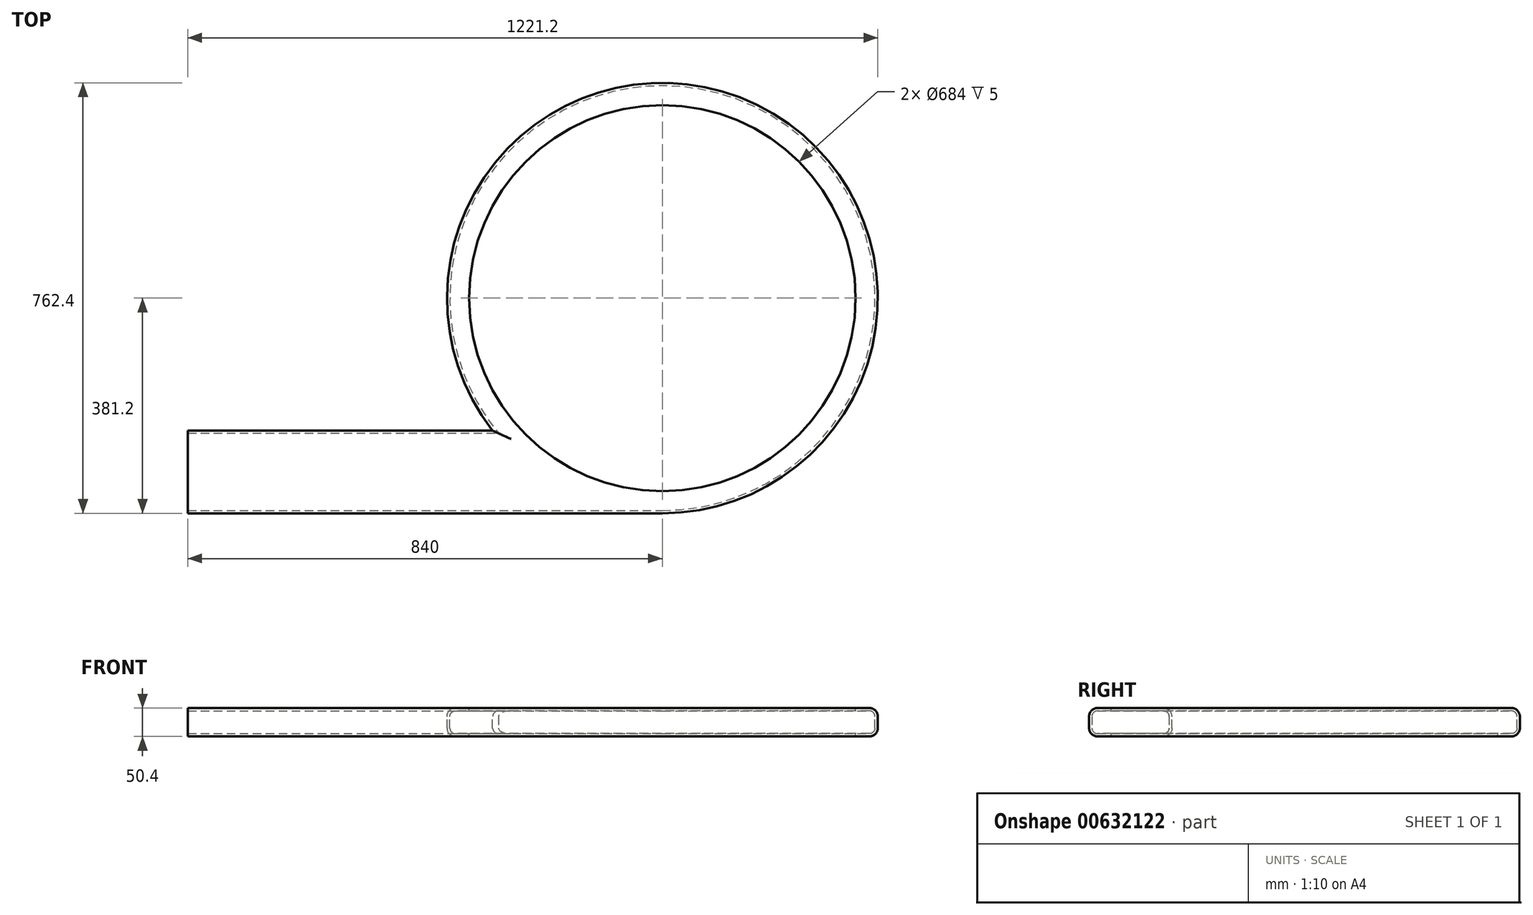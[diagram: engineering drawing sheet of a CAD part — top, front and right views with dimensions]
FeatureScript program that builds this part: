
annotation { "Feature Type Name" : "Feature", "Feature Type Description" : "" }
export const myFeature = defineFeature(function(context is Context, id is Id, definition is map)
    precondition{}
    {
        {
            var Q0;
            Q0=qCreatedBy(makeId("Top.planeOp"),FACE);
            var sketch = newSketch(context, id + "F0", { "sketchPlane" : qUnion([Q0])});
            skPoint(sketch, "E0", {"position": v(120, 0) * mm});
            skPoint(sketch, "E1", {"position": v(120.43, 3.39) * mm});
            skPoint(sketch, "E2", {"position": v(120.87, 6.78) * mm});
            skPoint(sketch, "E3", {"position": v(121.31, 10.17) * mm});
            skPoint(sketch, "E4", {"position": v(121.75, 13.57) * mm});
            skPoint(sketch, "E5", {"position": v(122.19, 16.98) * mm});
            skPoint(sketch, "E6", {"position": v(122.63, 20.37) * mm});
            skPoint(sketch, "E7", {"position": v(124.7, 30.21) * mm});
            skPoint(sketch, "E8", {"position": v(126.32, 40.24) * mm});
            skPoint(sketch, "E9", {"position": v(127.2, 50.5) * mm});
            skPoint(sketch, "E10", {"position": v(127.28, 60.98) * mm});
            skPoint(sketch, "E11", {"position": v(126.55, 71.6) * mm});
            skPoint(sketch, "E12", {"position": v(125, 82.33) * mm});
            skPoint(sketch, "E13", {"position": v(122.6, 93.1) * mm});
            skPoint(sketch, "E14", {"position": v(119.4, 103.82) * mm});
            skPoint(sketch, "E15", {"position": v(115.32, 114.48) * mm});
            skPoint(sketch, "E16", {"position": v(110.46, 124.94) * mm});
            skPoint(sketch, "E17", {"position": v(104.8, 135.2) * mm});
            skPoint(sketch, "E18", {"position": v(98.37, 145.13) * mm});
            skPoint(sketch, "E19", {"position": v(91.24, 154.7) * mm});
            skPoint(sketch, "E20", {"position": v(83.43, 163.88) * mm});
            skPoint(sketch, "E21", {"position": v(74.97, 172.59) * mm});
            skPoint(sketch, "E22", {"position": v(65.98, 180.79) * mm});
            skPoint(sketch, "E23", {"position": v(56.5, 188.45) * mm});
            skPoint(sketch, "E24", {"position": v(46.55, 195.56) * mm});
            skPoint(sketch, "E25", {"position": v(43.8, 199.07) * mm});
            skPoint(sketch, "E26", {"position": v(41.13, 202.54) * mm});
            skPoint(sketch, "E27", {"position": v(38.47, 205.97) * mm});
            skSolve(sketch);
        }
        {
            var Q0;
            Q0=qCreatedBy(makeId("Top.planeOp"),FACE);
            var sketch = newSketch(context, id + "F1", { "sketchPlane" : qUnion([Q0])});
            skPoint(sketch, "E28", {"position": v(120, 0) * mm});
            skPoint(sketch, "E29", {"position": v(122.73, 2.49) * mm});
            skPoint(sketch, "E30", {"position": v(124.8, 5.43) * mm});
            skPoint(sketch, "E31", {"position": v(126.44, 9.06) * mm});
            skPoint(sketch, "E32", {"position": v(128.14, 12.11) * mm});
            skPoint(sketch, "E33", {"position": v(129.88, 15.23) * mm});
            skPoint(sketch, "E34", {"position": v(131.67, 18.41) * mm});
            skPoint(sketch, "E35", {"position": v(134.5, 28.24) * mm});
            skPoint(sketch, "E36", {"position": v(136.25, 39.02) * mm});
            skPoint(sketch, "E37", {"position": v(137.19, 50.04) * mm});
            skPoint(sketch, "E38", {"position": v(137.28, 61.26) * mm});
            skPoint(sketch, "E39", {"position": v(136.5, 72.67) * mm});
            skPoint(sketch, "E40", {"position": v(134.83, 84.12) * mm});
            skPoint(sketch, "E41", {"position": v(132.28, 95.62) * mm});
            skPoint(sketch, "E42", {"position": v(128.85, 107.05) * mm});
            skPoint(sketch, "E43", {"position": v(124.54, 118.35) * mm});
            skPoint(sketch, "E44", {"position": v(119.36, 129.49) * mm});
            skPoint(sketch, "E45", {"position": v(113.38, 140.32) * mm});
            skPoint(sketch, "E46", {"position": v(106.6, 150.83) * mm});
            skPoint(sketch, "E47", {"position": v(99.05, 160.94) * mm});
            skPoint(sketch, "E48", {"position": v(90.82, 170.6) * mm});
            skPoint(sketch, "E49", {"position": v(81.96, 179.76) * mm});
            skPoint(sketch, "E50", {"position": v(72.5, 188.38) * mm});
            skPoint(sketch, "E51", {"position": v(62.53, 196.42) * mm});
            skPoint(sketch, "E52", {"position": v(52.12, 203.86) * mm});
            skPoint(sketch, "E53", {"position": v(47.32, 204.95) * mm});
            skPoint(sketch, "E54", {"position": v(42.9, 205.94) * mm});
            skPoint(sketch, "E55", {"position": v(38.97, 206.83) * mm});
            skSolve(sketch);
        }
        {
            var Q0;
            Q0=qCreatedBy(makeId("Top.planeOp"),FACE);
            var sketch = newSketch(context, id + "F2", { "sketchPlane" : qUnion([Q0])});
            skPoint(sketch, "E56", {"position": v(120, 0) * mm});
            skPoint(sketch, "E57", {"position": v(120.43, 3.39) * mm});
            skPoint(sketch, "E58", {"position": v(120.87, 6.78) * mm});
            skPoint(sketch, "E59", {"position": v(121.31, 10.17) * mm});
            skPoint(sketch, "E60", {"position": v(121.75, 13.57) * mm});
            skPoint(sketch, "E61", {"position": v(122.19, 16.98) * mm});
            skPoint(sketch, "E62", {"position": v(122.63, 20.37) * mm});
            skPoint(sketch, "E63", {"position": v(124.7, 30.21) * mm});
            skPoint(sketch, "E64", {"position": v(126.32, 40.24) * mm});
            skPoint(sketch, "E65", {"position": v(127.2, 50.5) * mm});
            skPoint(sketch, "E66", {"position": v(127.28, 60.98) * mm});
            skPoint(sketch, "E67", {"position": v(126.55, 71.6) * mm});
            skPoint(sketch, "E68", {"position": v(125, 82.33) * mm});
            skPoint(sketch, "E69", {"position": v(122.6, 93.1) * mm});
            skPoint(sketch, "E70", {"position": v(119.4, 103.82) * mm});
            skPoint(sketch, "E71", {"position": v(115.32, 114.48) * mm});
            skPoint(sketch, "E72", {"position": v(110.46, 124.94) * mm});
            skPoint(sketch, "E73", {"position": v(104.8, 135.2) * mm});
            skPoint(sketch, "E74", {"position": v(98.37, 145.13) * mm});
            skPoint(sketch, "E75", {"position": v(91.24, 154.7) * mm});
            skPoint(sketch, "E76", {"position": v(83.43, 163.88) * mm});
            skPoint(sketch, "E77", {"position": v(74.97, 172.59) * mm});
            skPoint(sketch, "E78", {"position": v(65.98, 180.79) * mm});
            skPoint(sketch, "E79", {"position": v(56.5, 188.45) * mm});
            skPoint(sketch, "E80", {"position": v(46.55, 195.56) * mm});
            skPoint(sketch, "E81", {"position": v(43.8, 199.07) * mm});
            skPoint(sketch, "E82", {"position": v(41.13, 202.54) * mm});
            skPoint(sketch, "E83", {"position": v(38.47, 205.97) * mm});
            skFitSpline(sketch, "E84", {"points": [v(38.47, 205.97) * mm, v(41.13, 202.54) * mm, v(43.8, 199.07) * mm, v(46.55, 195.56) * mm, v(56.5, 188.45) * mm, v(65.98, 180.79) * mm, v(74.97, 172.59) * mm, v(83.43, 163.88) * mm, v(91.24, 154.7) * mm, v(98.37, 145.13) * mm, v(104.8, 135.2) * mm, v(110.46, 124.94) * mm, v(115.32, 114.48) * mm, v(119.4, 103.82) * mm, v(122.6, 93.1) * mm, v(125, 82.33) * mm, v(126.55, 71.6) * mm, v(127.28, 60.98) * mm, v(127.2, 50.5) * mm, v(126.32, 40.24) * mm, v(124.7, 30.21) * mm, v(122.63, 20.37) * mm, v(122.19, 16.98) * mm, v(121.75, 13.57) * mm, v(121.31, 10.17) * mm, v(120.87, 6.78) * mm, v(120.43, 3.39) * mm, v(120, 0) * mm], "startDerivative": vector(97.9, -127.8) * mm, "endDerivative": vector(-18.24, -142.78) * mm});
            skPoint(sketch, "E85", {"position": v(38.97, 206.83) * mm});
            skPoint(sketch, "E86", {"position": v(42.9, 205.94) * mm});
            skPoint(sketch, "E87", {"position": v(47.32, 204.95) * mm});
            skPoint(sketch, "E88", {"position": v(52.12, 203.86) * mm});
            skPoint(sketch, "E89", {"position": v(62.53, 196.42) * mm});
            skPoint(sketch, "E90", {"position": v(72.5, 188.38) * mm});
            skPoint(sketch, "E91", {"position": v(81.96, 179.76) * mm});
            skPoint(sketch, "E92", {"position": v(90.82, 170.6) * mm});
            skPoint(sketch, "E93", {"position": v(99.05, 160.94) * mm});
            skPoint(sketch, "E94", {"position": v(106.6, 150.83) * mm});
            skPoint(sketch, "E95", {"position": v(113.38, 140.32) * mm});
            skPoint(sketch, "E96", {"position": v(119.36, 129.49) * mm});
            skPoint(sketch, "E97", {"position": v(124.54, 118.35) * mm});
            skPoint(sketch, "E98", {"position": v(128.85, 107.05) * mm});
            skPoint(sketch, "E99", {"position": v(132.28, 95.62) * mm});
            skPoint(sketch, "E100", {"position": v(134.83, 84.12) * mm});
            skPoint(sketch, "E101", {"position": v(136.5, 72.67) * mm});
            skPoint(sketch, "E102", {"position": v(137.28, 61.26) * mm});
            skPoint(sketch, "E103", {"position": v(137.19, 50.04) * mm});
            skPoint(sketch, "E104", {"position": v(136.25, 39.02) * mm});
            skPoint(sketch, "E105", {"position": v(134.5, 28.24) * mm});
            skPoint(sketch, "E106", {"position": v(131.67, 18.41) * mm});
            skPoint(sketch, "E107", {"position": v(129.88, 15.23) * mm});
            skPoint(sketch, "E108", {"position": v(128.14, 12.11) * mm});
            skPoint(sketch, "E109", {"position": v(126.44, 9.06) * mm});
            skPoint(sketch, "E110", {"position": v(124.8, 5.43) * mm});
            skPoint(sketch, "E111", {"position": v(122.73, 2.49) * mm});
            skLineSegment(sketch, "E112", {"start": v(38.97, 206.83) * mm, "end": v(42.9, 205.94) * mm});
            skLineSegment(sketch, "E113", {"start": v(42.9, 205.94) * mm, "end": v(47.32, 204.95) * mm});
            skLineSegment(sketch, "E114", {"start": v(47.32, 204.95) * mm, "end": v(52.12, 203.86) * mm});
            skLineSegment(sketch, "E115", {"start": v(38.97, 206.83) * mm, "end": v(38.47, 205.97) * mm});
            skFitSpline(sketch, "E116", {"points": [v(120, 0) * mm, v(122.73, 2.49) * mm, v(124.8, 5.43) * mm, v(131.67, 18.41) * mm, v(134.5, 28.24) * mm, v(136.25, 39.02) * mm, v(137.19, 50.04) * mm, v(137.28, 61.26) * mm, v(136.5, 72.67) * mm, v(134.83, 84.12) * mm, v(132.28, 95.62) * mm, v(128.85, 107.05) * mm, v(124.54, 118.35) * mm, v(119.36, 129.49) * mm, v(113.38, 140.32) * mm, v(106.6, 150.83) * mm, v(99.05, 160.94) * mm, v(90.82, 170.6) * mm, v(81.96, 179.76) * mm, v(72.5, 188.38) * mm, v(62.53, 196.42) * mm, v(52.12, 203.86) * mm], "startDerivative": vector(108.95, 92.2) * mm, "endDerivative": vector(-205.44, 143.17) * mm});
            skSolve(sketch);
        }
        {
            var Q0;
            Q0 = qSketchRegion(id + "F2", true);
            extrude(context, id + "F3", {"entities" : qUnion([Q0]), "depth" : 20.2 * mm, "offsetDistance" : 25 * mm, "hasSecondDirection" : true, "secondDirectionOppositeDirection" : true, "secondDirectionDepth" : 20.2 * mm});
        }
        {
            var Q0;
            Q0=qCreatedBy(makeId("Right.planeOp"),FACE);
            var sketch = newSketch(context, id + "F4", { "sketchPlane" : qUnion([Q0])});
            skLineSegment(sketch, "E117", {"start": v(0, 0) * mm, "end": v(0, 50) * mm, "construction": true});
            skSolve(sketch);
        }
        {
            var Q0;
            Q0=makeQuery(id+"F3.opExtrude","SWEPT_EDGE",EDGE,{"disambiguationData":[OSD([sQuery(id+"F2.wireOp",EDGE,"E84"),sQuery(id+"F2.wireOp",EDGE,"E115")])]});
            var Q1;
            Q1=makeQuery(id+"F3.opExtrude","SWEPT_EDGE",EDGE,{"disambiguationData":[OSD([sQuery(id+"F2.wireOp",EDGE,"E112"),sQuery(id+"F2.wireOp",EDGE,"E115")])]});
            fillet(context, id + "F5", {"entities" : qUnion([Q0, Q1]), "radius" : 0.75 * mm, "tangentPropagation" : true, "allowEdgeOverflow" : false});
        }
        {
            var Q0;
            Q0=makeQuery(id+"F3.opExtrude","SWEPT_BODY",BODY,{"disambiguationData":[OSD([sQuery(id+"F2.wireOp",EDGE,"E84"),sQuery(id+"F2.wireOp",EDGE,"E112"),sQuery(id+"F2.wireOp",EDGE,"E113"),sQuery(id+"F2.wireOp",EDGE,"E114"),sQuery(id+"F2.wireOp",EDGE,"E115"),sQuery(id+"F2.wireOp",EDGE,"E116")])]});
            var Q1;
            Q1=sQuery(id+"F4.wireOp",EDGE,"E117");
            circularPattern(context, id + "F6", {"entities" : qUnion([Q0]), "axis" : qUnion([Q1]), "angle" : 360 * degree, "instanceCount" : 7, "equalSpace" : true});
        }
        {
            var Q0;
            Q0=qCreatedBy(makeId("Front.planeOp"),FACE);
            var sketch = newSketch(context, id + "F7", { "sketchPlane" : qUnion([Q0])});
            skLineSegment(sketch, "E118", {"start": v(92, -342) * mm, "end": v(92, -45.2) * mm});
            skArc(sketch, "E119", {"start": v(117, -20.2) * mm, "mid": v(99.32, -27.52) * mm, "end": v(92, -45.2) * mm});
            skLineSegment(sketch, "E120", {"start": v(117, -20.2) * mm, "end": v(342, -20.2) * mm});
            skLineSegment(sketch, "E121.0", {"start": v(117, -25.2) * mm, "end": v(342, -25.2) * mm});
            skArc(sketch, "E121.1", {"start": v(117, -25.2) * mm, "mid": v(102.86, -31.06) * mm, "end": v(97, -45.2) * mm});
            skLineSegment(sketch, "E121.2", {"start": v(97, -342) * mm, "end": v(97, -45.2) * mm});
            skLineSegment(sketch, "E122", {"start": v(342, -20.2) * mm, "end": v(342, -25.2) * mm});
            skLineSegment(sketch, "E123", {"start": v(92, -342) * mm, "end": v(97, -342) * mm});
            skLineSegment(sketch, "E124", {"start": v(0, 0) * mm, "end": v(0, -344.46) * mm, "construction": true});
            skLineSegment(sketch, "E125", {"start": v(342, 20.2) * mm, "end": v(120, 20.2) * mm});
            skArc(sketch, "E126", {"start": v(120, 20.2) * mm, "mid": v(54.05, -4.63) * mm, "end": v(20.85, -66.8) * mm});
            skArc(sketch, "E127", {"start": v(0, -92.8) * mm, "mid": v(14.06, -82.72) * mm, "end": v(20.85, -66.8) * mm});
            skLineSegment(sketch, "E128", {"start": v(342, 20.2) * mm, "end": v(342, 25.2) * mm});
            skLineSegment(sketch, "E129", {"start": v(342, 25.2) * mm, "end": v(0, 25.2) * mm});
            skLineSegment(sketch, "E130", {"start": v(0, 25.2) * mm, "end": v(0, -92.8) * mm});
            skSolve(sketch);
        }
        {
            var Q0;
            Q0=qCreatedBy(makeId("Top.planeOp"),FACE);
            var sketch = newSketch(context, id + "F8", { "sketchPlane" : qUnion([Q0])});
            skArc(sketch, "E131", {"start": v(129.63, -305.65) * mm, "mid": v(216.02, -164.93) * mm, "end": v(223.94, 0) * mm, "construction": true});
            skLineSegment(sketch, "E132", {"start": v(223.94, 0) * mm, "end": v(208.8, 73.45) * mm, "construction": true});
            skArc(sketch, "E133.0", {"start": v(132.4, -308.52) * mm, "mid": v(212.69, -186.86) * mm, "end": v(233.9, -42.65) * mm});
            skArc(sketch, "E134.0", {"start": v(126.85, -302.77) * mm, "mid": v(211.9, -164.71) * mm, "end": v(220.42, -2.78) * mm});
            skLineSegment(sketch, "E135", {"start": v(126.85, -302.77) * mm, "end": v(132.4, -308.52) * mm});
            skLineSegment(sketch, "E136", {"start": v(224.39, -1.93) * mm, "end": v(233.9, -42.65) * mm});
            skLineSegment(sketch, "E137", {"start": v(-101.22, -67.04) * mm, "end": v(129.63, -305.65) * mm, "construction": true});
            skLineSegment(sketch, "E138", {"start": v(-101.22, -67.04) * mm, "end": v(223.94, 0) * mm, "construction": true});
            skLineSegment(sketch, "E139", {"start": v(-101.22, -67.04) * mm, "end": v(229.9, -42.94) * mm, "construction": true});
            skLineSegment(sketch, "E140", {"start": v(229.9, -42.94) * mm, "end": v(233.9, -42.65) * mm, "construction": true});
            skArc(sketch, "E141", {"start": v(224.39, -1.93) * mm, "mid": v(221.98, -0.4) * mm, "end": v(220.42, -2.78) * mm});
            skSolve(sketch);
        }
        {
            var Q0;
            Q0=qCreatedBy(makeId("Right.planeOp"),FACE);
            var sketch = newSketch(context, id + "F9", { "sketchPlane" : qUnion([Q0])});
            skLineSegment(sketch, "E142.bottom", {"start": v(-342, -20.2) * mm, "end": v(-366.2, -20.2) * mm});
            skLineSegment(sketch, "E142.top", {"start": v(-342, 20.2) * mm, "end": v(-366.2, 20.2) * mm});
            skLineSegment(sketch, "E142.right", {"start": v(-376.2, -10.2) * mm, "end": v(-376.2, 10.2) * mm});
            skPoint(sketch, "E143.visualSharp", {"position": v(-376.2, 20.2) * mm});
            skArc(sketch, "E143.filletArc", {"start": v(-366.2, 20.2) * mm, "mid": v(-373.27, 17.27) * mm, "end": v(-376.2, 10.2) * mm});
            skPoint(sketch, "E144.visualSharp", {"position": v(-376.2, -20.2) * mm});
            skArc(sketch, "E144.filletArc", {"start": v(-376.2, -10.2) * mm, "mid": v(-373.27, -17.27) * mm, "end": v(-366.2, -20.2) * mm});
            skLineSegment(sketch, "E145", {"start": v(-342, 20.2) * mm, "end": v(-342, 25.2) * mm});
            skLineSegment(sketch, "E146", {"start": v(-342, 25.2) * mm, "end": v(-366.2, 25.2) * mm});
            skLineSegment(sketch, "E147", {"start": v(-381.2, 10.2) * mm, "end": v(-381.2, -10.2) * mm});
            skLineSegment(sketch, "E148", {"start": v(-366.2, -25.2) * mm, "end": v(-342, -25.2) * mm});
            skLineSegment(sketch, "E149", {"start": v(-342, -25.2) * mm, "end": v(-342, -20.2) * mm});
            skPoint(sketch, "E150.visualSharp", {"position": v(-381.2, 25.2) * mm});
            skArc(sketch, "E150.filletArc", {"start": v(-366.2, 25.2) * mm, "mid": v(-376.8, 20.8) * mm, "end": v(-381.2, 10.2) * mm});
            skPoint(sketch, "E151.visualSharp", {"position": v(-381.2, -25.2) * mm});
            skArc(sketch, "E151.filletArc", {"start": v(-381.2, -10.2) * mm, "mid": v(-376.8, -20.8) * mm, "end": v(-366.2, -25.2) * mm});
            skSolve(sketch);
        }
        {
            var Q0;
            Q0=makeQuery(id+"F9.imprint","IMPRINT",FACE,{"disambiguationData":[TD([[makeQuery(id+"F9.imprint","IMPRINT",EDGE,{"derivedFrom":sQuery(id+"F9.wireOp",EDGE,"E142.bottom")}),1.0]])]});
            var Q1;
            Q1=sQuery(id+"F7.wireOp",EDGE,"E124");
            revolve(context, id + "F10", {"entities" : qUnion([Q0]), "axis" : qUnion([Q1]), "revolveType" : RevolveType.FULL});
        }
        {
            var Q0;
            Q0=qCreatedBy(makeId("Right.planeOp"),FACE);
            var sketch = newSketch(context, id + "F11", { "sketchPlane" : qUnion([Q0])});
            skLineSegment(sketch, "E152.bottom", {"start": v(-249.4, 20.2) * mm, "end": v(-366.2, 20.2) * mm});
            skLineSegment(sketch, "E152.top", {"start": v(-249.4, -20.2) * mm, "end": v(-366.2, -20.2) * mm});
            skLineSegment(sketch, "E152.left", {"start": v(-239.4, 10.2) * mm, "end": v(-239.4, -10.2) * mm});
            skLineSegment(sketch, "E152.right", {"start": v(-376.2, 10.2) * mm, "end": v(-376.2, -10.2) * mm});
            skPoint(sketch, "E153.visualSharp", {"position": v(-376.2, 20.2) * mm});
            skArc(sketch, "E153.filletArc", {"start": v(-366.2, 20.2) * mm, "mid": v(-373.27, 17.27) * mm, "end": v(-376.2, 10.2) * mm});
            skPoint(sketch, "E154.visualSharp", {"position": v(-376.2, -20.2) * mm});
            skArc(sketch, "E154.filletArc", {"start": v(-376.2, -10.2) * mm, "mid": v(-373.27, -17.27) * mm, "end": v(-366.2, -20.2) * mm});
            skPoint(sketch, "E155.visualSharp", {"position": v(-239.4, -20.2) * mm});
            skArc(sketch, "E155.filletArc", {"start": v(-249.4, -20.2) * mm, "mid": v(-242.33, -17.27) * mm, "end": v(-239.4, -10.2) * mm});
            skPoint(sketch, "E156.visualSharp", {"position": v(-239.4, 20.2) * mm});
            skArc(sketch, "E156.filletArc", {"start": v(-239.4, 10.2) * mm, "mid": v(-242.33, 17.27) * mm, "end": v(-249.4, 20.2) * mm});
            skSolve(sketch);
        }
        {
            var Q0;
            Q0 = qSketchRegion(id + "F11", true);
            extrude(context, id + "F12", {"entities" : qUnion([Q0]), "operationType" : NewBodyOperationType.REMOVE, "endBound" : BoundingType.THROUGH_ALL, "oppositeDirection" : true, "depth" : 25 * mm, "offsetDistance" : 25 * mm});
        }
        {
            var Q0;
            Q0=qCreatedBy(makeId("Right.planeOp"),FACE);
            var sketch = newSketch(context, id + "F13", { "sketchPlane" : qUnion([Q0])});
            skLineSegment(sketch, "E157.bottom", {"start": v(-249.4, 20.2) * mm, "end": v(-366.2, 20.2) * mm});
            skLineSegment(sketch, "E157.top", {"start": v(-249.4, -20.2) * mm, "end": v(-366.2, -20.2) * mm});
            skLineSegment(sketch, "E157.left", {"start": v(-239.4, 10.2) * mm, "end": v(-239.4, -10.2) * mm});
            skLineSegment(sketch, "E157.right", {"start": v(-376.2, 10.2) * mm, "end": v(-376.2, -10.2) * mm});
            skPoint(sketch, "E158.visualSharp", {"position": v(-239.4, 20.2) * mm});
            skArc(sketch, "E158.filletArc", {"start": v(-239.4, 10.2) * mm, "mid": v(-242.33, 17.27) * mm, "end": v(-249.4, 20.2) * mm});
            skPoint(sketch, "E159.visualSharp", {"position": v(-239.4, -20.2) * mm});
            skArc(sketch, "E159.filletArc", {"start": v(-249.4, -20.2) * mm, "mid": v(-242.33, -17.27) * mm, "end": v(-239.4, -10.2) * mm});
            skPoint(sketch, "E160.visualSharp", {"position": v(-376.2, -20.2) * mm});
            skArc(sketch, "E160.filletArc", {"start": v(-376.2, -10.2) * mm, "mid": v(-373.27, -17.27) * mm, "end": v(-366.2, -20.2) * mm});
            skPoint(sketch, "E161.visualSharp", {"position": v(-376.2, 20.2) * mm});
            skArc(sketch, "E161.filletArc", {"start": v(-366.2, 20.2) * mm, "mid": v(-373.27, 17.27) * mm, "end": v(-376.2, 10.2) * mm});
            skArc(sketch, "E162.0", {"start": v(-234.4, 10.2) * mm, "mid": v(-238.8, 20.8) * mm, "end": v(-249.4, 25.2) * mm});
            skLineSegment(sketch, "E162.1", {"start": v(-234.4, 10.2) * mm, "end": v(-234.4, -10.2) * mm});
            skLineSegment(sketch, "E162.2", {"start": v(-249.4, 25.2) * mm, "end": v(-366.2, 25.2) * mm});
            skArc(sketch, "E162.3", {"start": v(-249.4, -25.2) * mm, "mid": v(-238.8, -20.8) * mm, "end": v(-234.4, -10.2) * mm});
            skArc(sketch, "E162.4", {"start": v(-366.2, 25.2) * mm, "mid": v(-376.8, 20.8) * mm, "end": v(-381.2, 10.2) * mm});
            skLineSegment(sketch, "E162.5", {"start": v(-381.2, 10.2) * mm, "end": v(-381.2, -10.2) * mm});
            skArc(sketch, "E162.6", {"start": v(-381.2, -10.2) * mm, "mid": v(-376.8, -20.8) * mm, "end": v(-366.2, -25.2) * mm});
            skLineSegment(sketch, "E162.7", {"start": v(-249.4, -25.2) * mm, "end": v(-366.2, -25.2) * mm});
            skSolve(sketch);
        }
        {
            var Q0;
            Q0 = qSketchRegion(id + "F13", true);
            extrude(context, id + "F14", {"entities" : qUnion([Q0]), "operationType" : NewBodyOperationType.ADD, "oppositeDirection" : true, "depth" : 840 * mm, "offsetDistance" : 25 * mm});
        }
        {
            var Q0;
            Q0=qCreatedBy(makeId("Right.planeOp"),FACE);
            var sketch = newSketch(context, id + "F15", { "sketchPlane" : qUnion([Q0])});
            skLineSegment(sketch, "E163.bottom", {"start": v(-234.4, 20.2) * mm, "end": v(-366.2, 20.2) * mm});
            skLineSegment(sketch, "E163.top", {"start": v(-234.4, -20.2) * mm, "end": v(-366.2, -20.2) * mm});
            skLineSegment(sketch, "E163.left", {"start": v(-234.4, 20.2) * mm, "end": v(-234.4, -20.2) * mm});
            skLineSegment(sketch, "E163.right", {"start": v(-376.2, 10.2) * mm, "end": v(-376.2, -10.2) * mm});
            skPoint(sketch, "E164.visualSharp", {"position": v(-376.2, -20.2) * mm});
            skArc(sketch, "E164.filletArc", {"start": v(-376.2, -10.2) * mm, "mid": v(-373.27, -17.27) * mm, "end": v(-366.2, -20.2) * mm});
            skPoint(sketch, "E165.visualSharp", {"position": v(-376.2, 20.2) * mm});
            skArc(sketch, "E165.filletArc", {"start": v(-366.2, 20.2) * mm, "mid": v(-373.27, 17.27) * mm, "end": v(-376.2, 10.2) * mm});
            skSolve(sketch);
        }
        {
            var Q0;
            Q0 = qSketchRegion(id + "F15", true);
            var Q1;
            Q1=sQuery(id+"F7.wireOp",EDGE,"E124");
            revolve(context, id + "F16", {"operationType" : NewBodyOperationType.REMOVE, "entities" : qUnion([Q0]), "axis" : qUnion([Q1]), "revolveType" : RevolveType.FULL, "oppositeDirection" : true});
        }
        {
            var Q0;
            Q0 = qSketchRegion(id + "F8", true);
            extrude(context, id + "F17", {"entities" : qUnion([Q0]), "depth" : 20.2 * mm, "offsetDistance" : 25 * mm, "hasSecondDirection" : true, "secondDirectionOppositeDirection" : true, "secondDirectionDepth" : 20.2 * mm});
        }
        {
            var Q0;
            Q0=makeQuery(id+"F17.opExtrude","SWEPT_BODY",BODY,{"disambiguationData":[OSD([sQuery(id+"F8.wireOp",EDGE,"E133.0"),sQuery(id+"F8.wireOp",EDGE,"E134.0"),sQuery(id+"F8.wireOp",EDGE,"E135"),sQuery(id+"F8.wireOp",EDGE,"E136"),sQuery(id+"F8.wireOp",EDGE,"E141")])]});
            var Q1;
            Q1=sQuery(id+"F7.wireOp",EDGE,"E124");
            circularPattern(context, id + "F18", {"entities" : qUnion([Q0]), "axis" : qUnion([Q1]), "angle" : 360 * degree, "instanceCount" : 12, "equalSpace" : true});
        }
        {
            var Q0;
            Q0 = qSketchRegion(id + "F7", true);
            var Q1;
            Q1=sQuery(id+"F7.wireOp",EDGE,"E124");
            revolve(context, id + "F19", {"entities" : qUnion([Q0]), "axis" : qUnion([Q1]), "revolveType" : RevolveType.FULL});
        }
        {
            var Q0;
            Q0=qCreatedBy(makeId("Top.planeOp"),FACE);
            var sketch = newSketch(context, id + "F20", { "sketchPlane" : qUnion([Q0])});
            skCircle(sketch, "E166", {"center": v(0, 0) * mm, "radius": 342 * mm});
            skSolve(sketch);
        }
        {
            var Q0;
            Q0 = qSketchRegion(id + "F20", true);
            extrude(context, id + "F21", {"entities" : qUnion([Q0]), "operationType" : NewBodyOperationType.REMOVE, "endBound" : BoundingType.THROUGH_ALL, "oppositeDirection" : true, "depth" : 25 * mm, "offsetDistance" : 25 * mm, "hasSecondDirection" : true, "secondDirectionBound" : SecondDirectionBoundingType.THROUGH_ALL, "secondDirectionOppositeDirection" : false, "secondDirectionDepth" : 25 * mm});
        }
    });
